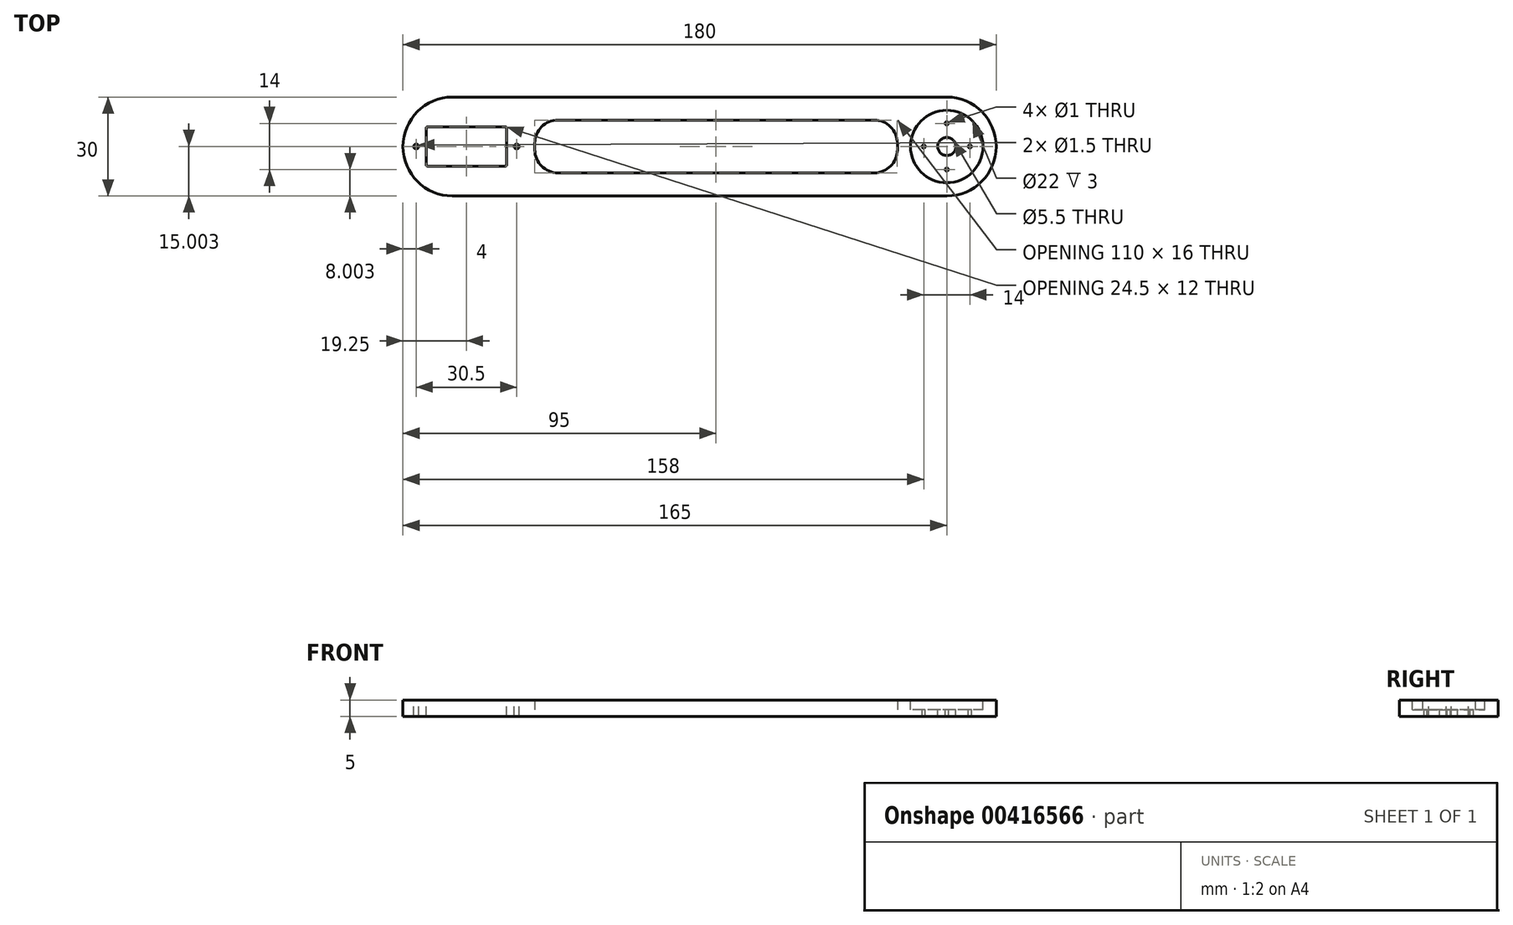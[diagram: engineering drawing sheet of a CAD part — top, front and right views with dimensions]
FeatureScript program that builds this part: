
annotation { "Feature Type Name" : "Feature", "Feature Type Description" : "" }
export const myFeature = defineFeature(function(context is Context, id is Id, definition is map)
    precondition{}
    {
        {
            var Q0;
            Q0=qCreatedBy(makeId("Top.planeOp"),FACE);
            var sketch = newSketch(context, id + "F0", { "sketchPlane" : qUnion([Q0])});
            skLineSegment(sketch, "E0.bottom", {"start": v(-80, 3.1) * mm, "end": v(100, 3.1) * mm});
            skLineSegment(sketch, "E0.top", {"start": v(-80, -26.9) * mm, "end": v(100, -26.9) * mm});
            skLineSegment(sketch, "E0.left", {"start": v(-80, 3.1) * mm, "end": v(-80, -26.9) * mm});
            skLineSegment(sketch, "E0.right", {"start": v(100, 3.1) * mm, "end": v(100, -26.9) * mm});
            skLineSegment(sketch, "E1.bottom", {"start": v(-40, -3.9) * mm, "end": v(70, -3.9) * mm});
            skLineSegment(sketch, "E1.top", {"start": v(-40, -19.9) * mm, "end": v(70, -19.9) * mm});
            skLineSegment(sketch, "E1.left", {"start": v(-40, -3.9) * mm, "end": v(-40, -19.9) * mm});
            skLineSegment(sketch, "E1.right", {"start": v(70, -3.9) * mm, "end": v(70, -19.9) * mm});
            skSolve(sketch);
        }
        {
            var Q0;
            Q0=makeQuery(id+"F0.imprint","IMPRINT",FACE,{"disambiguationData":[TD([[makeQuery(id+"F0.imprint","IMPRINT",EDGE,{"derivedFrom":sQuery(id+"F0.wireOp",EDGE,"E0.bottom")}),-1.0]])]});
            extrude(context, id + "F1", {"entities" : qUnion([Q0]), "depth" : 5 * mm});
        }
        {
            var Q0;
            Q0=makeQuery(id+"F1.opExtrude","CAP_FACE",FACE,{"disambiguationData":[OSD([sQuery(id+"F0.wireOp",EDGE,"E0.bottom"),sQuery(id+"F0.wireOp",EDGE,"E0.top"),sQuery(id+"F0.wireOp",EDGE,"E0.left"),sQuery(id+"F0.wireOp",EDGE,"E0.right")])],"isStart":false});
            var sketch = newSketch(context, id + "F2", { "sketchPlane" : qUnion([Q0])});
            skCircle(sketch, "E2", {"center": v(85, -11.9) * mm, "radius": 11 * mm});
            skCircle(sketch, "E3", {"center": v(85, -11.9) * mm, "radius": 2.75 * mm});
            skCircle(sketch, "E4", {"center": v(85, -4.9) * mm, "radius": 0.5 * mm});
            skCircle(sketch, "E5", {"center": v(85, -18.9) * mm, "radius": 0.5 * mm});
            skCircle(sketch, "E6", {"center": v(92, -11.9) * mm, "radius": 0.5 * mm});
            skCircle(sketch, "E7", {"center": v(78, -11.9) * mm, "radius": 0.5 * mm});
            skCircle(sketch, "E8", {"center": v(-65, -11.9) * mm, "radius": 2.75 * mm});
            skLineSegment(sketch, "E9.bottom", {"start": v(-73, -5.9) * mm, "end": v(-48.5, -5.9) * mm});
            skLineSegment(sketch, "E9.top", {"start": v(-73, -17.9) * mm, "end": v(-48.5, -17.9) * mm});
            skLineSegment(sketch, "E9.left", {"start": v(-73, -5.9) * mm, "end": v(-73, -17.9) * mm});
            skLineSegment(sketch, "E9.right", {"start": v(-48.5, -5.9) * mm, "end": v(-48.5, -17.9) * mm});
            skCircle(sketch, "E10", {"center": v(-45.5, -11.9) * mm, "radius": 0.75 * mm});
            skCircle(sketch, "E11", {"center": v(-76, -11.9) * mm, "radius": 0.75 * mm});
            skSolve(sketch);
        }
        {
            var Q0;
            Q0=makeQuery(id+"F2.imprint","IMPRINT",FACE,{"disambiguationData":[TD([[makeQuery(id+"F2.imprint","IMPRINT",EDGE,{"derivedFrom":sQuery(id+"F2.wireOp",EDGE,"E2")}),1.0]])]});
            var Q1;
            Q1=makeQuery(id+"F2.imprint","IMPRINT",FACE,{"disambiguationData":[TD([[makeQuery(id+"F2.imprint","IMPRINT",EDGE,{"derivedFrom":sQuery(id+"F2.wireOp",EDGE,"E8")}),-1.0]])]});
            extrude(context, id + "F3", {"entities" : qUnion([Q0, Q1]), "operationType" : NewBodyOperationType.REMOVE, "oppositeDirection" : true, "depth" : 3 * mm});
        }
        {
            var Q0;
            Q0=makeQuery(id+"F2.imprint","IMPRINT",FACE,{"disambiguationData":[TD([[makeQuery(id+"F2.imprint","IMPRINT",EDGE,{"derivedFrom":sQuery(id+"F2.wireOp",EDGE,"E3")}),1.0]])]});
            var Q1;
            Q1=makeQuery(id+"F2.imprint","IMPRINT",FACE,{"disambiguationData":[TD([[makeQuery(id+"F2.imprint","IMPRINT",EDGE,{"derivedFrom":sQuery(id+"F2.wireOp",EDGE,"E4")}),1.0]])]});
            var Q2;
            Q2=makeQuery(id+"F2.imprint","IMPRINT",FACE,{"disambiguationData":[TD([[makeQuery(id+"F2.imprint","IMPRINT",EDGE,{"derivedFrom":sQuery(id+"F2.wireOp",EDGE,"E7")}),1.0]])]});
            var Q3;
            Q3=makeQuery(id+"F2.imprint","IMPRINT",FACE,{"disambiguationData":[TD([[makeQuery(id+"F2.imprint","IMPRINT",EDGE,{"derivedFrom":sQuery(id+"F2.wireOp",EDGE,"E5")}),1.0]])]});
            var Q4;
            Q4=makeQuery(id+"F2.imprint","IMPRINT",FACE,{"disambiguationData":[TD([[makeQuery(id+"F2.imprint","IMPRINT",EDGE,{"derivedFrom":sQuery(id+"F2.wireOp",EDGE,"E6")}),1.0]])]});
            var Q5;
            Q5=makeQuery(id+"F2.imprint","IMPRINT",FACE,{"disambiguationData":[TD([[makeQuery(id+"F2.imprint","IMPRINT",EDGE,{"derivedFrom":sQuery(id+"F2.wireOp",EDGE,"E8")}),1.0]])]});
            var Q6;
            Q6=makeQuery(id+"F2.imprint","IMPRINT",FACE,{"disambiguationData":[TD([[makeQuery(id+"F2.imprint","IMPRINT",EDGE,{"derivedFrom":sQuery(id+"F2.wireOp",EDGE,"BxBnCqye-svmn-VfxW-Yds5-lMc6FiJJZGoG")}),1.0]])]});
            var Q7;
            Q7=makeQuery(id+"F2.imprint","IMPRINT",FACE,{"disambiguationData":[TD([[makeQuery(id+"F2.imprint","IMPRINT",EDGE,{"derivedFrom":sQuery(id+"F2.wireOp",EDGE,"Fvn0a9T8-UYAr-KfxW-xJAN-rbL94ZbWyBAD")}),1.0]])]});
            var Q8;
            Q8=makeQuery(id+"F2.imprint","IMPRINT",FACE,{"disambiguationData":[TD([[makeQuery(id+"F2.imprint","IMPRINT",EDGE,{"derivedFrom":sQuery(id+"F2.wireOp",EDGE,"IbQh5voC-LfIl-WeLM-aWEU-xkcyqfmnFLrg")}),1.0]])]});
            var Q9;
            Q9=makeQuery(id+"F2.imprint","IMPRINT",FACE,{"disambiguationData":[TD([[makeQuery(id+"F2.imprint","IMPRINT",EDGE,{"derivedFrom":sQuery(id+"F2.wireOp",EDGE,"Jml5Gy1f-vHH9-9BCY-gYTi-q249JlMg9aTh")}),1.0]])]});
            var Q10;
            Q10=makeQuery(id+"F2.imprint","IMPRINT",FACE,{"disambiguationData":[TD([[makeQuery(id+"F2.imprint","IMPRINT",EDGE,{"derivedFrom":sQuery(id+"F2.wireOp",EDGE,"E8")}),-1.0]])]});
            var Q11;
            Q11=makeQuery(id+"F2.imprint","IMPRINT",FACE,{"disambiguationData":[TD([[makeQuery(id+"F2.imprint","IMPRINT",EDGE,{"derivedFrom":sQuery(id+"F2.wireOp",EDGE,"E11")}),1.0]])]});
            var Q12;
            Q12=makeQuery(id+"F2.imprint","IMPRINT",FACE,{"disambiguationData":[TD([[makeQuery(id+"F2.imprint","IMPRINT",EDGE,{"derivedFrom":sQuery(id+"F2.wireOp",EDGE,"E10")}),1.0]])]});
            extrude(context, id + "F4", {"entities" : qUnion([Q0, Q1, Q2, Q3, Q4, Q5, Q6, Q7, Q8, Q9, Q10, Q11, Q12]), "operationType" : NewBodyOperationType.REMOVE, "oppositeDirection" : true, "depth" : 25 * mm});
        }
        {
            var Q0;
            Q0=makeQuery(id+"F1.opExtrude","SWEPT_EDGE",EDGE,{"disambiguationData":[OSD([sQuery(id+"F0.wireOp",EDGE,"E0.bottom"),sQuery(id+"F0.wireOp",EDGE,"E0.right")])]});
            var Q1;
            Q1=makeQuery(id+"F1.opExtrude","SWEPT_EDGE",EDGE,{"disambiguationData":[OSD([sQuery(id+"F0.wireOp",EDGE,"E0.top"),sQuery(id+"F0.wireOp",EDGE,"E0.right")])]});
            var Q2;
            Q2=makeQuery(id+"F1.opExtrude","SWEPT_EDGE",EDGE,{"disambiguationData":[OSD([sQuery(id+"F0.wireOp",EDGE,"E0.top"),sQuery(id+"F0.wireOp",EDGE,"E0.left")])]});
            var Q3;
            Q3=makeQuery(id+"F1.opExtrude","SWEPT_EDGE",EDGE,{"disambiguationData":[OSD([sQuery(id+"F0.wireOp",EDGE,"E0.bottom"),sQuery(id+"F0.wireOp",EDGE,"E0.left")])]});
            fillet(context, id + "F5", {"entities" : qUnion([Q0, Q1, Q2, Q3]), "radius" : 15 * mm, "tangentPropagation" : true, "allowEdgeOverflow" : false});
        }
        {
            var Q0;
            Q0=makeQuery(id+"F1.opExtrude","SWEPT_EDGE",EDGE,{"disambiguationData":[OSD([sQuery(id+"F0.wireOp",EDGE,"E1.bottom"),sQuery(id+"F0.wireOp",EDGE,"E1.left")])]});
            var Q1;
            Q1=makeQuery(id+"F1.opExtrude","SWEPT_EDGE",EDGE,{"disambiguationData":[OSD([sQuery(id+"F0.wireOp",EDGE,"E1.top"),sQuery(id+"F0.wireOp",EDGE,"E1.left")])]});
            var Q2;
            Q2=makeQuery(id+"F1.opExtrude","SWEPT_EDGE",EDGE,{"disambiguationData":[OSD([sQuery(id+"F0.wireOp",EDGE,"E1.bottom"),sQuery(id+"F0.wireOp",EDGE,"E1.right")])]});
            var Q3;
            Q3=makeQuery(id+"F1.opExtrude","SWEPT_EDGE",EDGE,{"disambiguationData":[OSD([sQuery(id+"F0.wireOp",EDGE,"E1.top"),sQuery(id+"F0.wireOp",EDGE,"E1.right")])]});
            fillet(context, id + "F6", {"entities" : qUnion([Q0, Q1, Q2, Q3]), "radius" : 7 * mm, "tangentPropagation" : true, "allowEdgeOverflow" : false});
        }
        {
            var Q0;
            {var subQ0=sQuery(id+"F2.wireOp",EDGE,"E9.left");var subQ1=sQuery(id+"F2.wireOp",EDGE,"E9.bottom");Q0=makeQuery(id+"F4.boolean.opBoolean","MERGE",EDGE,{"derivedFrom":[makeQuery(id+"F3.boolean.opBoolean","COPY",EDGE,{"derivedFrom":makeQuery(id+"F3.opExtrude","SWEPT_EDGE",EDGE,{"disambiguationData":[OSD([subQ1,subQ0])]})}),makeQuery(id+"F4.opExtrude","SWEPT_EDGE",EDGE,{"disambiguationData":[OSD([subQ1,subQ0])]})]});}
            var Q1;
            {var subQ0=sQuery(id+"F2.wireOp",EDGE,"E9.left");var subQ1=sQuery(id+"F2.wireOp",EDGE,"E9.top");Q1=makeQuery(id+"F4.boolean.opBoolean","MERGE",EDGE,{"derivedFrom":[makeQuery(id+"F3.boolean.opBoolean","COPY",EDGE,{"derivedFrom":makeQuery(id+"F3.opExtrude","SWEPT_EDGE",EDGE,{"disambiguationData":[OSD([subQ1,subQ0])]})}),makeQuery(id+"F4.opExtrude","SWEPT_EDGE",EDGE,{"disambiguationData":[OSD([subQ1,subQ0])]})]});}
            var Q2;
            {var subQ0=sQuery(id+"F2.wireOp",EDGE,"E9.right");var subQ1=sQuery(id+"F2.wireOp",EDGE,"E9.bottom");Q2=makeQuery(id+"F4.boolean.opBoolean","MERGE",EDGE,{"derivedFrom":[makeQuery(id+"F3.boolean.opBoolean","COPY",EDGE,{"derivedFrom":makeQuery(id+"F3.opExtrude","SWEPT_EDGE",EDGE,{"disambiguationData":[OSD([subQ1,subQ0])]})}),makeQuery(id+"F4.opExtrude","SWEPT_EDGE",EDGE,{"disambiguationData":[OSD([subQ1,subQ0])]})]});}
            var Q3;
            {var subQ0=sQuery(id+"F2.wireOp",EDGE,"E9.right");var subQ1=sQuery(id+"F2.wireOp",EDGE,"E9.top");Q3=makeQuery(id+"F4.boolean.opBoolean","MERGE",EDGE,{"derivedFrom":[makeQuery(id+"F3.boolean.opBoolean","COPY",EDGE,{"derivedFrom":makeQuery(id+"F3.opExtrude","SWEPT_EDGE",EDGE,{"disambiguationData":[OSD([subQ1,subQ0])]})}),makeQuery(id+"F4.opExtrude","SWEPT_EDGE",EDGE,{"disambiguationData":[OSD([subQ1,subQ0])]})]});}
            fillet(context, id + "F7", {"entities" : qUnion([Q0, Q1, Q2, Q3]), "radius" : 0.5 * mm, "tangentPropagation" : true, "allowEdgeOverflow" : false});
        }
    });
